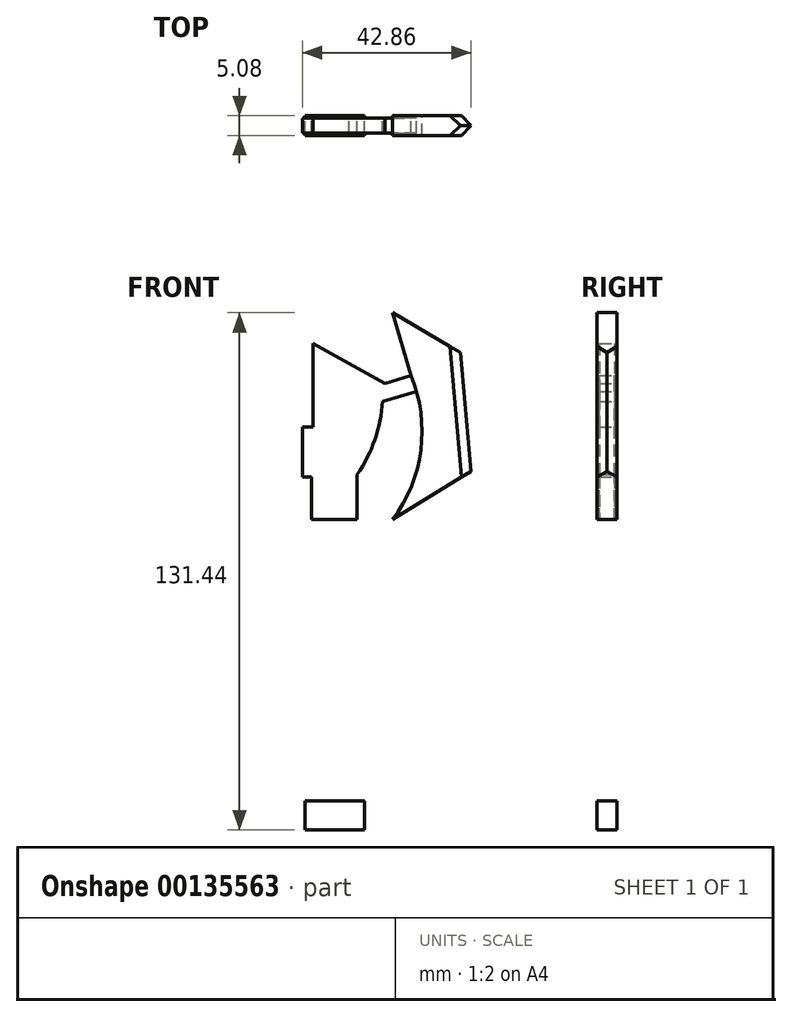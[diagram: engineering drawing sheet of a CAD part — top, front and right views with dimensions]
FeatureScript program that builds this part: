
annotation { "Feature Type Name" : "Feature", "Feature Type Description" : "" }
export const myFeature = defineFeature(function(context is Context, id is Id, definition is map)
    precondition{}
    {
        {
            var Q0;
            Q0=qCreatedBy(makeId("Front.planeOp"),FACE);
            var sketch = newSketch(context, id + "F0", { "sketchPlane" : qUnion([Q0])});
            skLineSegment(sketch, "E0", {"start": v(-20.17, 44.75) * mm, "end": v(-1.93, 34.62) * mm});
            skLineSegment(sketch, "E1", {"start": v(-1.93, 34.62) * mm, "end": v(4.71, 36.57) * mm});
            skLineSegment(sketch, "E2", {"start": v(4.71, 36.57) * mm, "end": v(0, 52.6) * mm});
            skLineSegment(sketch, "E3", {"start": v(0, 52.6) * mm, "end": v(18.6, 41.62) * mm});
            skLineSegment(sketch, "E4", {"start": v(18.6, 41.62) * mm, "end": v(21.15, 13.02) * mm});
            skLineSegment(sketch, "E5", {"start": v(21.15, 13.02) * mm, "end": v(0, 0) * mm});
            skArc(sketch, "E6", {"start": v(0, 0) * mm, "mid": v(7.17, 17.67) * mm, "end": v(4.71, 36.57) * mm});
            skLineSegment(sketch, "E7", {"start": v(6.07, 32.61) * mm, "end": v(-2.53, 30.08) * mm});
            skLineSegment(sketch, "E8", {"start": v(-20.17, 44.75) * mm, "end": v(-20.17, 23.6) * mm});
            skLineSegment(sketch, "E9", {"start": v(-20.57, 10.87) * mm, "end": v(-20.57, 0) * mm});
            skLineSegment(sketch, "E10", {"start": v(-9, 0) * mm, "end": v(-9, 11.46) * mm});
            skArc(sketch, "E11", {"start": v(-9, 11.46) * mm, "mid": v(-4.52, 20.34) * mm, "end": v(-2.53, 30.08) * mm});
            skLineSegment(sketch, "E12", {"start": v(-20.17, 23.6) * mm, "end": v(-22.92, 23.6) * mm});
            skLineSegment(sketch, "E13", {"start": v(-22.92, 23.6) * mm, "end": v(-22.92, 10.87) * mm});
            skLineSegment(sketch, "E14", {"start": v(-22.92, 10.87) * mm, "end": v(-20.57, 10.87) * mm});
            skLineSegment(sketch, "E15", {"start": v(-20.57, 0) * mm, "end": v(-18.23, 0) * mm});
            skLineSegment(sketch, "E16", {"start": v(-9, 0) * mm, "end": v(-11.35, 0) * mm});
            skLineSegment(sketch, "E17.bottom", {"start": v(-18.23, 0) * mm, "end": v(-11.64, 0) * mm});
            skLineSegment(sketch, "E17.top", {"start": v(-18.23, -38.8) * mm, "end": v(-11.64, -38.8) * mm});
            skLineSegment(sketch, "E17.left", {"start": v(-18.23, 0) * mm, "end": v(-18.23, -38.8) * mm});
            skLineSegment(sketch, "E17.right", {"start": v(-11.64, 0) * mm, "end": v(-11.64, -38.8) * mm});
            skLineSegment(sketch, "E18", {"start": v(-11.64, 0) * mm, "end": v(-11.35, 0) * mm});
            skLineSegment(sketch, "E19", {"start": v(-18.23, -38.8) * mm, "end": v(-20.17, -38.8) * mm});
            skLineSegment(sketch, "E20", {"start": v(-20.17, -38.8) * mm, "end": v(-20.17, -51.02) * mm});
            skLineSegment(sketch, "E21", {"start": v(-20.17, -51.02) * mm, "end": v(-9.2, -51.02) * mm});
            skLineSegment(sketch, "E22", {"start": v(-9.2, -51.02) * mm, "end": v(-9.2, -38.8) * mm});
            skLineSegment(sketch, "E23", {"start": v(-9.2, -38.8) * mm, "end": v(-11.64, -38.8) * mm});
            skLineSegment(sketch, "E24.bottom", {"start": v(-18.35, -51.02) * mm, "end": v(-11.13, -51.02) * mm});
            skLineSegment(sketch, "E24.top", {"start": v(-18.35, -51.02) * mm, "end": v(-11.13, -51.02) * mm});
            skLineSegment(sketch, "E24.left", {"start": v(-18.35, -51.02) * mm, "end": v(-18.35, -51.02) * mm});
            skLineSegment(sketch, "E24.right", {"start": v(-11.13, -51.02) * mm, "end": v(-11.13, -51.02) * mm});
            skLineSegment(sketch, "E25.bottom", {"start": v(-11.13, -51.02) * mm, "end": v(-18.35, -51.02) * mm});
            skLineSegment(sketch, "E25.top", {"start": v(-11.13, -71.4) * mm, "end": v(-18.35, -71.4) * mm});
            skLineSegment(sketch, "E25.left", {"start": v(-11.13, -51.02) * mm, "end": v(-11.13, -71.4) * mm});
            skLineSegment(sketch, "E25.right", {"start": v(-18.35, -51.02) * mm, "end": v(-18.35, -71.4) * mm});
            skLineSegment(sketch, "E26", {"start": v(-18.35, -71.4) * mm, "end": v(-22.2, -71.4) * mm});
            skLineSegment(sketch, "E27", {"start": v(-22.2, -71.4) * mm, "end": v(-22.2, -78.84) * mm});
            skLineSegment(sketch, "E28", {"start": v(-22.2, -78.84) * mm, "end": v(-7.17, -78.84) * mm});
            skLineSegment(sketch, "E29", {"start": v(-7.17, -78.84) * mm, "end": v(-7.17, -71.5) * mm});
            skLineSegment(sketch, "E30", {"start": v(-7.17, -71.5) * mm, "end": v(-11.13, -71.4) * mm});
            skLineSegment(sketch, "E31", {"start": v(-14.94, 0) * mm, "end": v(-14.94, -38.8) * mm});
            skLineSegment(sketch, "E32", {"start": v(-14.94, -38.8) * mm, "end": v(-14.69, -51.02) * mm});
            skLineSegment(sketch, "E33", {"start": v(-14.69, -51.02) * mm, "end": v(-14.74, -71.4) * mm});
            skLineSegment(sketch, "E34", {"start": v(-14.74, -71.4) * mm, "end": v(-14.74, -78.84) * mm});
            skSolve(sketch);
        }
        {
            var Q0;
            Q0=sQuery(id+"F0.wireOp",EDGE,"E17.left");
            var Q1;
            Q1=sQuery(id+"F0.wireOp",EDGE,"E25.right");
            var Q2;
            Q2=sQuery(id+"F0.wireOp",EDGE,"E31");
            revolve(context, id + "F1", {"bodyType" : ToolBodyType.SURFACE, "surfaceEntities" : qUnion([Q0, Q1]), "axis" : qUnion([Q2]), "revolveType" : RevolveType.FULL});
        }
        {
            var Q0;
            Q0=sQuery(id+"F0.wireOp",EDGE,"E20");
            var Q1;
            Q1=sQuery(id+"F0.wireOp",EDGE,"E32");
            revolve(context, id + "F2", {"bodyType" : ToolBodyType.SURFACE, "surfaceEntities" : qUnion([Q0]), "axis" : qUnion([Q1]), "revolveType" : RevolveType.FULL});
        }
        {
            var Q0;
            Q0=makeQuery(id+"F0.imprint","IMPRINT",FACE,{"disambiguationData":[TD([[makeQuery(id+"F0.imprint","IMPRINT",EDGE,{"derivedFrom":sQuery(id+"F0.wireOp",EDGE,"E0")}),-1.0]])]});
            extrude(context, id + "F3", {"entities" : qUnion([Q0]), "endBound" : BoundingType.SYMMETRIC, "depth" : 3.8 * mm});
        }
        {
            var Q0;
            {var subQ1=sQuery(id+"F0.wireOp",EDGE,"E2");Q0=makeQuery(id+"F0.imprint","IMPRINT",FACE,{"disambiguationData":[TD([[makeQuery(id+"F0.imprint","IMPRINT",EDGE,{"derivedFrom":subQ1}),-1.0]])]});}
            extrude(context, id + "F4", {"entities" : qUnion([Q0]), "operationType" : NewBodyOperationType.ADD, "endBound" : BoundingType.SYMMETRIC, "depth" : 5.08 * mm});
        }
        {
            var Q0;
            Q0=makeQuery(id+"F4.opExtrude","CAP_EDGE",EDGE,{"disambiguationData":[OSD([sQuery(id+"F0.wireOp",EDGE,"E4")])],"isStart":false});
            var Q1;
            Q1=makeQuery(id+"F4.opExtrude","CAP_EDGE",EDGE,{"disambiguationData":[OSD([sQuery(id+"F0.wireOp",EDGE,"E4")])],"isStart":true});
            chamfer(context, id + "F5", {"entities" : qUnion([Q0, Q1]), "width" : 3.8 * mm, "tangentPropagation" : true});
        }
        {
            var Q0;
            {var subQ3=sQuery(id+"F0.wireOp",EDGE,"E26");Q0=makeQuery(id+"F0.imprint","IMPRINT",FACE,{"disambiguationData":[TD([[makeQuery(id+"F0.imprint","IMPRINT",EDGE,{"derivedFrom":subQ3}),1.0]])]});}
            var Q1;
            {var subQ1=sQuery(id+"F0.wireOp",EDGE,"E29");Q1=makeQuery(id+"F0.imprint","IMPRINT",FACE,{"disambiguationData":[TD([[makeQuery(id+"F0.imprint","IMPRINT",EDGE,{"derivedFrom":subQ1}),1.0]])]});}
            extrude(context, id + "F6", {"entities" : qUnion([Q0, Q1]), "endBound" : BoundingType.SYMMETRIC, "depth" : 5.08 * mm});
        }
        {
            var Q0;
            Q0=sQuery(id+"F0.wireOp",EDGE,"E27");
            var Q1;
            Q1=sQuery(id+"F0.wireOp",EDGE,"E34");
            revolve(context, id + "F7", {"bodyType" : ToolBodyType.SURFACE, "surfaceEntities" : qUnion([Q0]), "axis" : qUnion([Q1]), "revolveType" : RevolveType.FULL});
        }
    });
